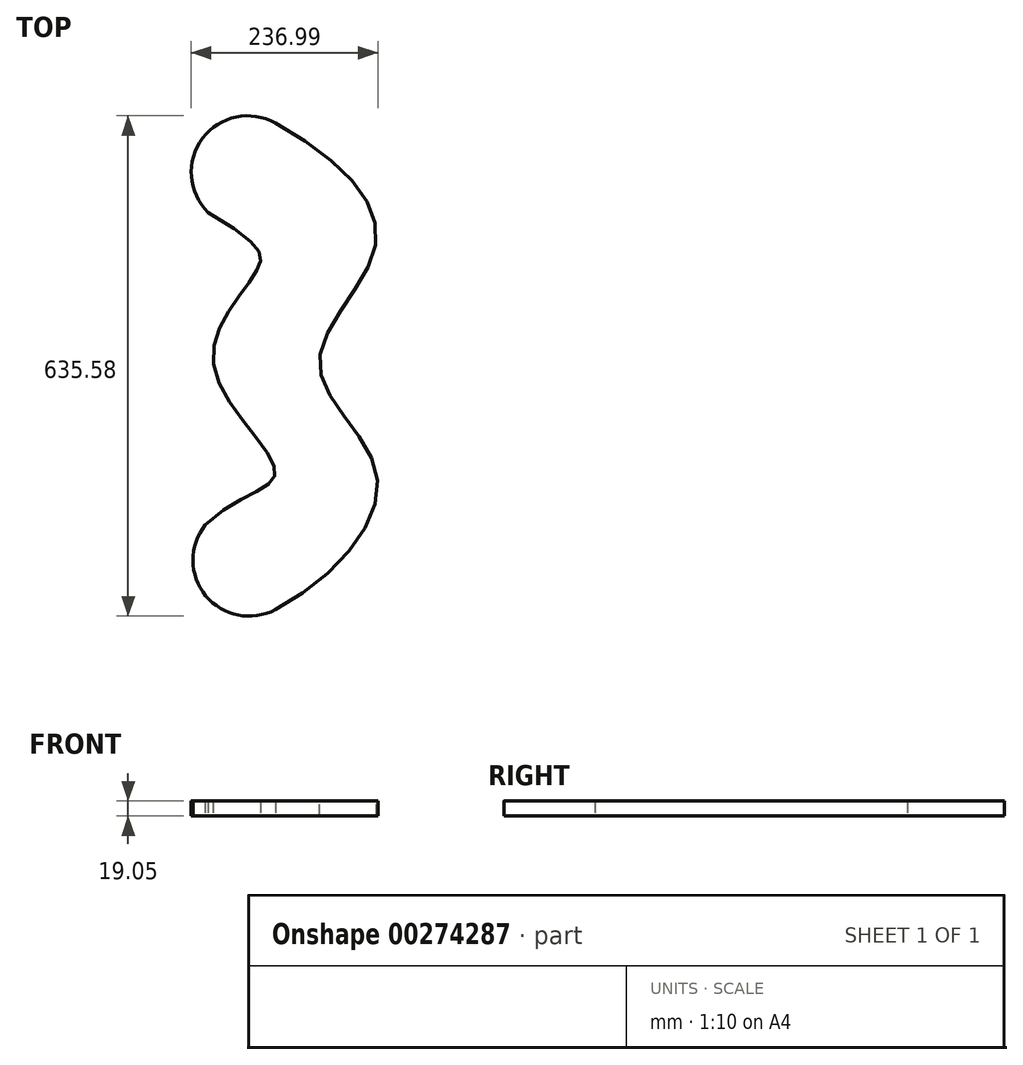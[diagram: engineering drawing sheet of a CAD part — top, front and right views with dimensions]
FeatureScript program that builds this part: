
annotation { "Feature Type Name" : "Feature", "Feature Type Description" : "" }
export const myFeature = defineFeature(function(context is Context, id is Id, definition is map)
    precondition{}
    {
        {
            var Q0;
            Q0=qCreatedBy(makeId("Top.planeOp"),FACE);
            var sketch = newSketch(context, id + "F0", { "sketchPlane" : qUnion([Q0])});
            skFitSpline(sketch, "E0", {"points": [v(0, 306.4) * mm, v(127.37, 151.93) * mm, v(55.94, 0) * mm, v(129.39, -142.46) * mm, v(0, -311.76) * mm], "startDerivative": vector(924.35, -518.82) * mm, "endDerivative": vector(-817.22, -431.93) * mm});
            skFitSpline(sketch, "E1", {"points": [v(-85.36, 192.84) * mm, v(-24.52, 117.12) * mm, v(-78.58, 0) * mm, v(0, -136.13) * mm, v(-88.96, -204.17) * mm], "startDerivative": vector(908.03, -547.25) * mm, "endDerivative": vector(-530.66, -504.75) * mm});
            skArc(sketch, "E2", {"start": v(0, 306.4) * mm, "mid": v(-92.36, 286.96) * mm, "end": v(-85.36, 192.84) * mm});
            skArc(sketch, "E3", {"start": v(-88.96, -204.17) * mm, "mid": v(-88.25, -294.16) * mm, "end": v(0, -311.76) * mm});
            skFitSpline(sketch, "E4", {"points": [v(-35.08, 243.9) * mm, v(53.25, 137.99) * mm, v(0, 0.67) * mm, v(68.63, -137.98) * mm, v(-30.34, -249.51) * mm], "startDerivative": vector(905.9, -550.64) * mm, "endDerivative": vector(-792.26, -480.7) * mm});
            skSolve(sketch);
        }
        {
            var Q0;
            Q0=makeQuery(id+"F0.imprint","IMPRINT",FACE,{"disambiguationData":[TD([[makeQuery(id+"F0.imprint","IMPRINT",EDGE,{"derivedFrom":sQuery(id+"F0.wireOp",EDGE,"E0")}),-1.0]])]});
            extrude(context, id + "F1", {"entities" : qUnion([Q0]), "depth" : 19.05 * mm});
        }
        {
            var Q0;
            Q0=qCreatedBy(makeId("Top.planeOp"),FACE);
            cPlane(context, id + "F2", {"entities" : qUnion([Q0]), "cplaneType" : CPlaneType.OFFSET, "offset" : 19.05 * mm, "width" : 152.4 * mm, "height" : 152.4 * mm});
        }
    });
